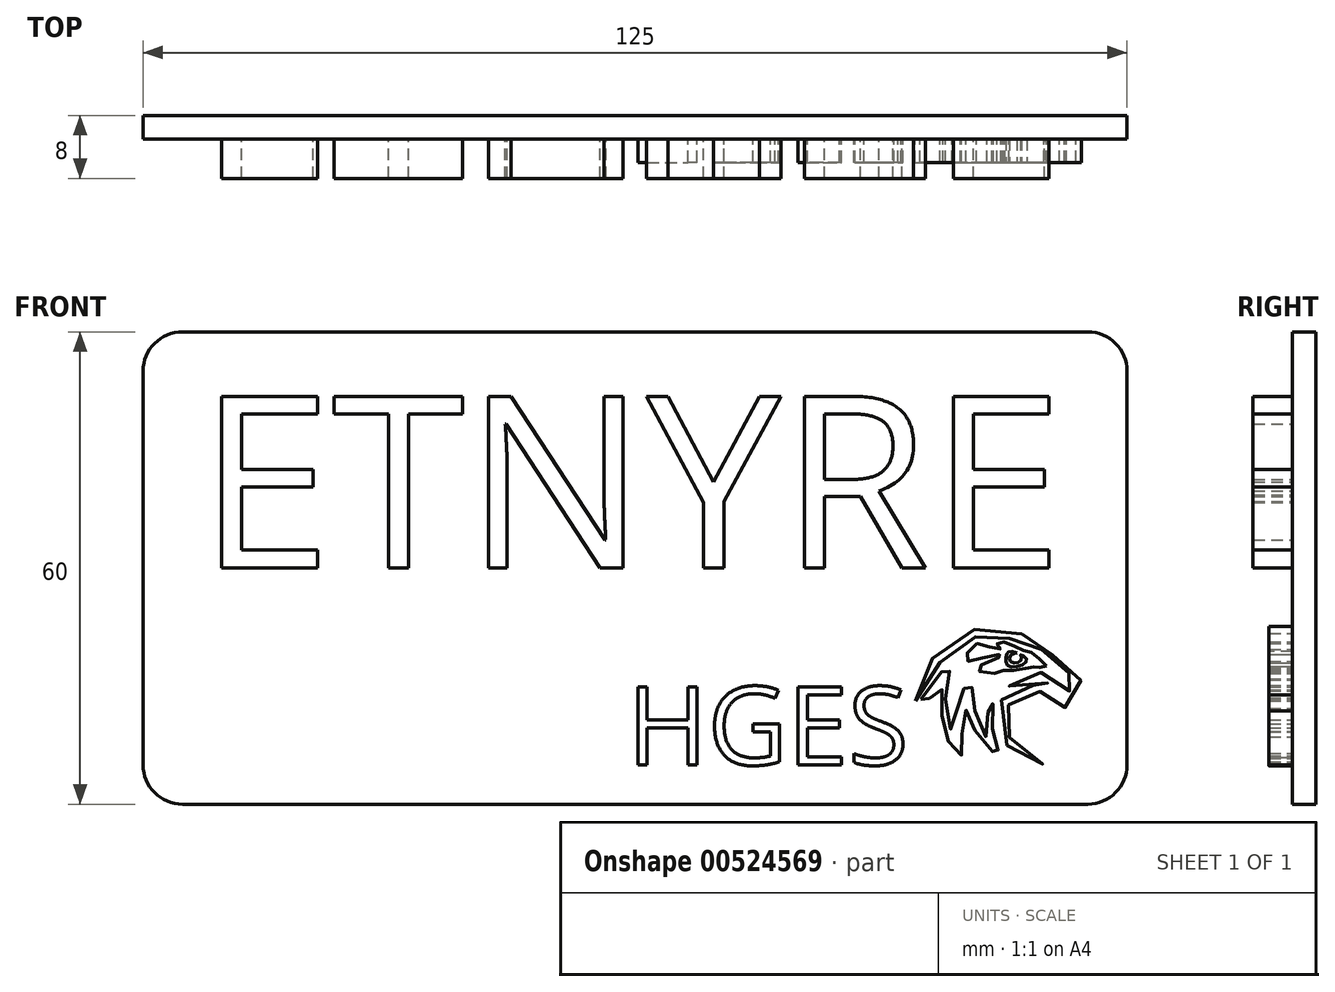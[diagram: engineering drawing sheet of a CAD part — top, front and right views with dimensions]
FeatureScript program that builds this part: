
annotation { "Feature Type Name" : "Feature", "Feature Type Description" : "" }
export const myFeature = defineFeature(function(context is Context, id is Id, definition is map)
    precondition{}
    {
        {
            var Q0;
            Q0=qCreatedBy(makeId("Front.planeOp"),FACE);
            var sketch = newSketch(context, id + "F0", { "sketchPlane" : qUnion([Q0])});
            skLineSegment(sketch, "E0.bottom", {"start": v(-75, 45) * mm, "end": v(50, 45) * mm});
            skLineSegment(sketch, "E0.top", {"start": v(-75, -15) * mm, "end": v(50, -15) * mm});
            skLineSegment(sketch, "E0.left", {"start": v(-75, 45) * mm, "end": v(-75, -15) * mm});
            skLineSegment(sketch, "E0.right", {"start": v(50, 45) * mm, "end": v(50, -15) * mm});
            skSolve(sketch);
        }
        {
            var Q0;
            Q0=makeQuery(id+"F0.imprint","IMPRINT",FACE,{"disambiguationData":[TD([[makeQuery(id+"F0.imprint","IMPRINT",EDGE,{"derivedFrom":sQuery(id+"F0.wireOp",EDGE,"E0.bottom")}),-1.0]])]});
            extrude(context, id + "F1", {"entities" : qUnion([Q0]), "oppositeDirection" : true, "depth" : 3 * mm});
        }
        {
            var Q0;
            Q0=makeQuery(id+"F1.opExtrude","CAP_FACE",FACE,{"disambiguationData":[OSD([sQuery(id+"F0.wireOp",EDGE,"E0.bottom"),sQuery(id+"F0.wireOp",EDGE,"E0.top"),sQuery(id+"F0.wireOp",EDGE,"E0.left"),sQuery(id+"F0.wireOp",EDGE,"E0.right")])],"isStart":true});
            var sketch = newSketch(context, id + "F2", { "sketchPlane" : qUnion([Q0])});
            skText(sketch, "E1", { "text": "HGES", "fontName": "OpenSans-Regular.ttf"});
            const initialGuessF2  = {"E1": [-0.01351, -0.01, 1, 0, 0.01]};
            skSetInitialGuess(sketch, initialGuessF2);
            skSolve(sketch);
        }
        {
            var Q0;
            Q0=qSketchRegion(id+"F2",true);
            extrude(context, id + "F3", {"entities" : qUnion([Q0]), "operationType" : NewBodyOperationType.ADD, "depth" : 3 * mm});
        }
        {
            var Q0;
            Q0=makeQuery(id+"F1.opExtrude","CAP_FACE",FACE,{"disambiguationData":[OSD([sQuery(id+"F0.wireOp",EDGE,"E0.bottom"),sQuery(id+"F0.wireOp",EDGE,"E0.top"),sQuery(id+"F0.wireOp",EDGE,"E0.left"),sQuery(id+"F0.wireOp",EDGE,"E0.right")])],"isStart":true});
            var sketch = newSketch(context, id + "F4", { "sketchPlane" : qUnion([Q0])});
            skFitSpline(sketch, "E2", {"points": [v(23.82, -1.68) * mm, v(26, 1.34) * mm, v(27.75, 2.92) * mm, v(27.33, 1.5) * mm, v(26.91, -1) * mm, v(27.24, -3.93) * mm, v(27.75, -5.77) * mm, v(28.08, -4.35) * mm, v(28.67, -1.76) * mm, v(29.42, 0) * mm, v(30.09, 0.92) * mm, v(30.34, -0.92) * mm, v(30.5, -2.43) * mm, v(31.1, -4.52) * mm, v(32.1, -6.44) * mm, v(32.18, -4.27) * mm, v(32.6, -2.43) * mm, v(32.76, -1.76) * mm, v(33.02, -2.93) * mm, v(32.85, -5.02) * mm, v(33.1, -6.61) * mm, v(33.6, -8.12) * mm, v(34.02, -9.2) * mm, v(32.68, -8.12) * mm, v(31.1, -6.28) * mm, v(30.09, -4.18) * mm, v(29.59, -3.01) * mm, v(29.08, -4.6) * mm, v(29, -6.53) * mm, v(28.83, -7.86) * mm, v(28.92, -9.04) * mm, v(27.75, -7.78) * mm, v(26.91, -5.86) * mm, v(26.4, -3.43) * mm, v(26.33, -1) * mm, v(26.58, 0) * mm, v(25.49, -0.76) * mm, v(23.82, -2.85) * mm, v(23.82, -1.68) * mm]});
            skSolve(sketch);
        }
        {
            var Q0;
            Q0=qSketchRegion(id+"F4",true);
            extrude(context, id + "F5", {"entities" : qUnion([Q0]), "operationType" : NewBodyOperationType.ADD, "depth" : 3 * mm});
        }
        {
            var Q0;
            Q0=makeQuery(id+"F1.opExtrude","CAP_FACE",FACE,{"disambiguationData":[OSD([sQuery(id+"F0.wireOp",EDGE,"E0.bottom"),sQuery(id+"F0.wireOp",EDGE,"E0.top"),sQuery(id+"F0.wireOp",EDGE,"E0.left"),sQuery(id+"F0.wireOp",EDGE,"E0.right")])],"isStart":true});
            var sketch = newSketch(context, id + "F6", { "sketchPlane" : qUnion([Q0])});
            skFitSpline(sketch, "E3", {"points": [v(23.1, -1.86) * mm, v(23.81, 0.98) * mm, v(25.7, 3.98) * mm, v(28.86, 6.43) * mm, v(33.05, 7.54) * mm, v(36.28, 6.67) * mm, v(39.13, 5.8) * mm, v(40.23, 4.23) * mm, v(41.97, 3.12) * mm, v(43.79, 1.46) * mm, v(43.87, -1.22) * mm, v(42.05, -3.11) * mm, v(42.3, -1.77) * mm, v(40.95, -0.83) * mm, v(38.5, -0.67) * mm, v(37.08, -0.67) * mm, v(35.03, -2.25) * mm, v(34.48, -3.83) * mm, v(34.63, -5.33) * mm, v(36.21, -7.85) * mm, v(39.45, -9.75) * mm, v(37.87, -9.9) * mm, v(35.43, -8.33) * mm, v(33.84, -5.96) * mm, v(33.84, -2.1) * mm, v(35.74, -0.6) * mm, v(37, 0) * mm, v(39.84, 0) * mm, v(41.42, 0) * mm, v(37.54, 0.73) * mm, v(35.86, 0.49) * mm, v(35.02, 0) * mm, v(35.55, 1.01) * mm, v(38.46, 1.74) * mm, v(40.54, 1.44) * mm, v(42.25, 0.55) * mm, v(42.92, -1.14) * mm, v(43.47, 0) * mm, v(42.92, 1.39) * mm, v(40.7, 2.88) * mm, v(39.29, 4.23) * mm, v(38.9, 5.02) * mm, v(37.4, 5.49) * mm, v(35.02, 6.04) * mm, v(33.36, 6.67) * mm, v(31.39, 6.43) * mm, v(28.78, 5.4) * mm, v(26.42, 3.2) * mm, v(25.15, 1.7) * mm, v(23.1, -1.86) * mm]});
            skSolve(sketch);
        }
        {
            var Q0;
            Q0=qSketchRegion(id+"F6",true);
            extrude(context, id + "F7", {"entities" : qUnion([Q0]), "operationType" : NewBodyOperationType.ADD, "depth" : 3 * mm});
        }
        {
            var Q0;
            Q0=makeQuery(id+"F1.opExtrude","CAP_FACE",FACE,{"disambiguationData":[OSD([sQuery(id+"F0.wireOp",EDGE,"E0.bottom"),sQuery(id+"F0.wireOp",EDGE,"E0.top"),sQuery(id+"F0.wireOp",EDGE,"E0.left"),sQuery(id+"F0.wireOp",EDGE,"E0.right")])],"isStart":true});
            var sketch = newSketch(context, id + "F8", { "sketchPlane" : qUnion([Q0])});
            skFitSpline(sketch, "E4", {"points": [v(39.76, 2.54) * mm, v(39.1, 2.36) * mm, v(38.4, 2.36) * mm, v(37.87, 2.49) * mm, v(36.1, 2) * mm, v(34.4, 2) * mm, v(33.02, 1.62) * mm, v(30.9, 2.21) * mm, v(34.18, 3.9) * mm, v(32.13, 3.7) * mm, v(29.55, 3.3) * mm, v(30.65, 5.3) * mm, v(32.97, 4.78) * mm, v(33.99, 4.8) * mm, v(33.44, 5.49) * mm, v(35.02, 5.4) * mm, v(36.4, 4.67) * mm, v(37.56, 4.4) * mm, v(38.58, 3.67) * mm, v(39.76, 2.54) * mm]});
            skSolve(sketch);
        }
        {
            var Q0;
            Q0=qSketchRegion(id+"F8",true);
            extrude(context, id + "F9", {"entities" : qUnion([Q0]), "operationType" : NewBodyOperationType.ADD, "depth" : 3 * mm});
        }
        {
            var Q0;
            Q0=makeQuery(id+"F9.opExtrude","CAP_FACE",FACE,{"disambiguationData":[OSD([sQuery(id+"F8.wireOp",EDGE,"E4")])],"isStart":false});
            var sketch = newSketch(context, id + "F10", { "sketchPlane" : qUnion([Q0])});
            skFitSpline(sketch, "E5", {"points": [v(36.02, 4.2) * mm, v(35.66, 4.34) * mm, v(34.89, 4.34) * mm, v(34.65, 3.77) * mm, v(34.83, 2.62) * mm, v(36.6, 2.65) * mm, v(37.22, 3.46) * mm, v(36.47, 3.96) * mm, v(36.6, 3.54) * mm, v(36.01, 2.94) * mm, v(35.12, 3.2) * mm, v(35.31, 4) * mm, v(36.02, 4.2) * mm]});
            skSolve(sketch);
        }
        {
            var Q0;
            Q0=qSketchRegion(id+"F10",true);
            extrude(context, id + "F11", {"entities" : qUnion([Q0]), "operationType" : NewBodyOperationType.REMOVE, "oppositeDirection" : true, "depth" : 3 * mm});
        }
        {
            var Q0;
            Q0=makeQuery(id+"F1.opExtrude","SWEPT_EDGE",EDGE,{"disambiguationData":[OSD([sQuery(id+"F0.wireOp",EDGE,"E0.bottom"),sQuery(id+"F0.wireOp",EDGE,"E0.left")])]});
            var Q1;
            Q1=makeQuery(id+"F1.opExtrude","SWEPT_EDGE",EDGE,{"disambiguationData":[OSD([sQuery(id+"F0.wireOp",EDGE,"E0.top"),sQuery(id+"F0.wireOp",EDGE,"E0.right")])]});
            var Q2;
            Q2=makeQuery(id+"F1.opExtrude","SWEPT_EDGE",EDGE,{"disambiguationData":[OSD([sQuery(id+"F0.wireOp",EDGE,"E0.bottom"),sQuery(id+"F0.wireOp",EDGE,"E0.right")])]});
            var Q3;
            Q3=makeQuery(id+"F1.opExtrude","SWEPT_EDGE",EDGE,{"disambiguationData":[OSD([sQuery(id+"F0.wireOp",EDGE,"E0.top"),sQuery(id+"F0.wireOp",EDGE,"E0.left")])]});
            fillet(context, id + "F12", {"entities" : qUnion([Q0, Q1, Q2, Q3]), "radius" : 5 * mm, "tangentPropagation" : true, "allowEdgeOverflow" : false});
        }
        {
            var Q0;
            Q0=makeQuery(id+"F1.opExtrude","CAP_FACE",FACE,{"disambiguationData":[OSD([sQuery(id+"F0.wireOp",EDGE,"E0.bottom"),sQuery(id+"F0.wireOp",EDGE,"E0.top"),sQuery(id+"F0.wireOp",EDGE,"E0.left"),sQuery(id+"F0.wireOp",EDGE,"E0.right")])],"isStart":true});
            var sketch = newSketch(context, id + "F13", { "sketchPlane" : qUnion([Q0])});
            skText(sketch, "E6", { "text": "ETNYRE", "fontName": "OpenSans-Regular.ttf"});
            const initialGuessF13  = {"E6": [-0.068, 0.015, 1, 0, 0.022]};
            skSetInitialGuess(sketch, initialGuessF13);
            skSolve(sketch);
        }
        {
            var Q0;
            Q0 = qSketchRegion(id + "F13", true);
            extrude(context, id + "F14", {"entities" : qUnion([Q0]), "operationType" : NewBodyOperationType.ADD, "depth" : 5 * mm, "offsetDistance" : 25 * mm});
        }
    });
